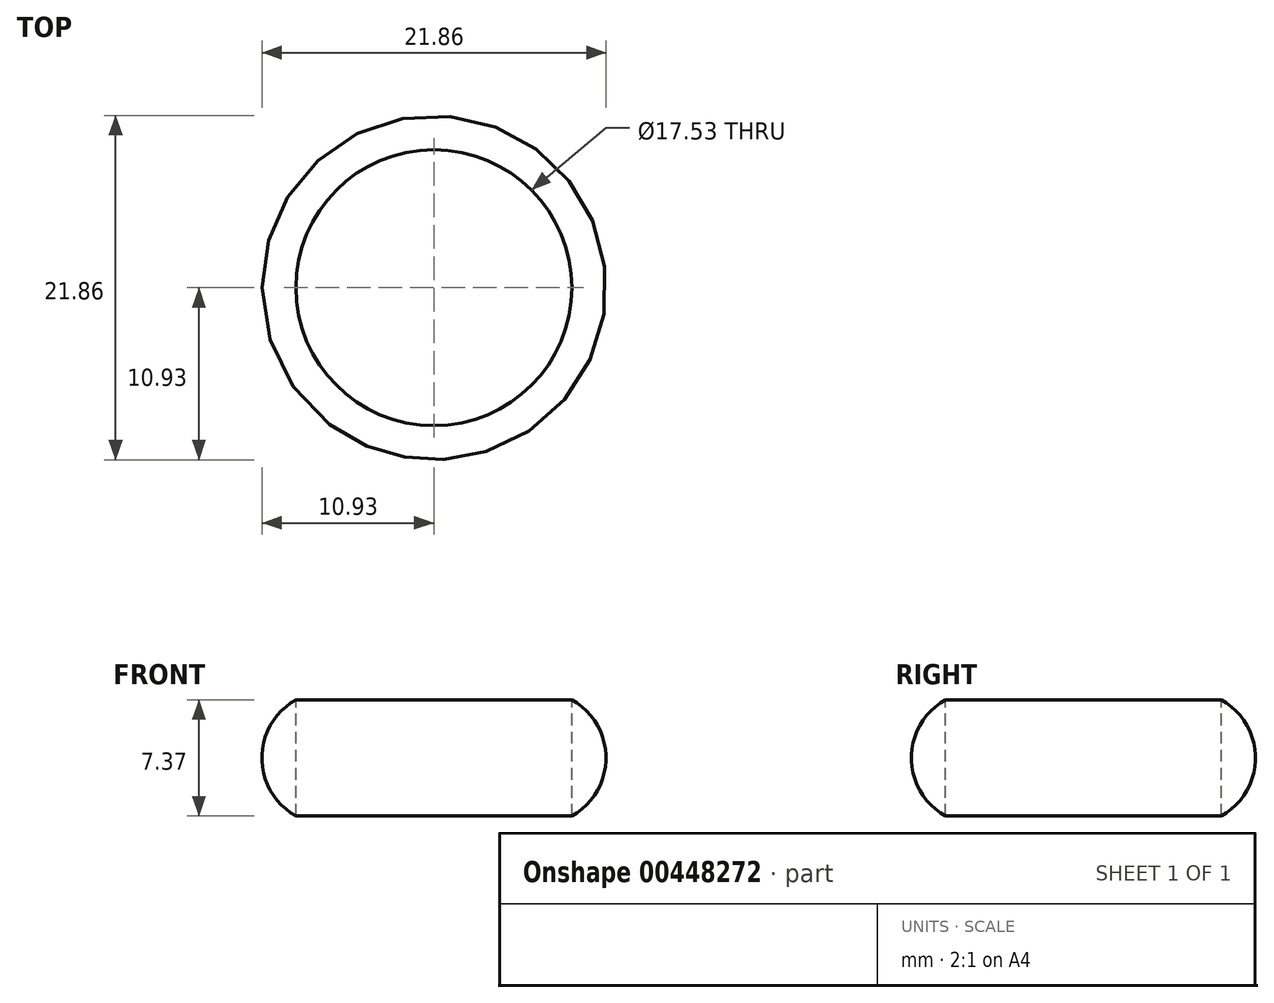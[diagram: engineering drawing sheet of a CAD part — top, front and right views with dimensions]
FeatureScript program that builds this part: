
annotation { "Feature Type Name" : "Feature", "Feature Type Description" : "" }
export const myFeature = defineFeature(function(context is Context, id is Id, definition is map)
    precondition{}
    {
        {
            var Q0;
            Q0=qCreatedBy(makeId("Top.planeOp"),FACE);
            var sketch = newSketch(context, id + "F0", { "sketchPlane" : qUnion([Q0])});
            skCircle(sketch, "E0", {"center": v(0, 0) * mm, "radius": 8.57 * mm});
            skSolve(sketch);
        }
        {
            var Q0;
            Q0=qCreatedBy(makeId("Front.planeOp"),FACE);
            var sketch = newSketch(context, id + "F1", { "sketchPlane" : qUnion([Q0])});
            skLineSegment(sketch, "E1", {"start": v(0, 0) * mm, "end": v(-8.76, 0) * mm});
            skLineSegment(sketch, "E2", {"start": v(-8.76, 0) * mm, "end": v(-8.76, 7.37) * mm});
            skArc(sketch, "E3", {"start": v(-8.76, 7.37) * mm, "mid": v(-10.93, 3.68) * mm, "end": v(-8.76, 0) * mm});
            skSolve(sketch);
        }
        {
            var Q0;
            Q0=makeQuery(id+"F1.imprint","IMPRINT",FACE,{"disambiguationData":[TD([[makeQuery(id+"F1.imprint","IMPRINT",EDGE,{"derivedFrom":sQuery(id+"F1.wireOp",EDGE,"E2")}),1.0]])]});
            var Q1;
            Q1=sQuery(id+"F0.wireOp",EDGE,"E0");
            sweep(context, id + "F2", {"profiles" : qUnion([Q0]), "path" : qUnion([Q1])});
        }
    });
